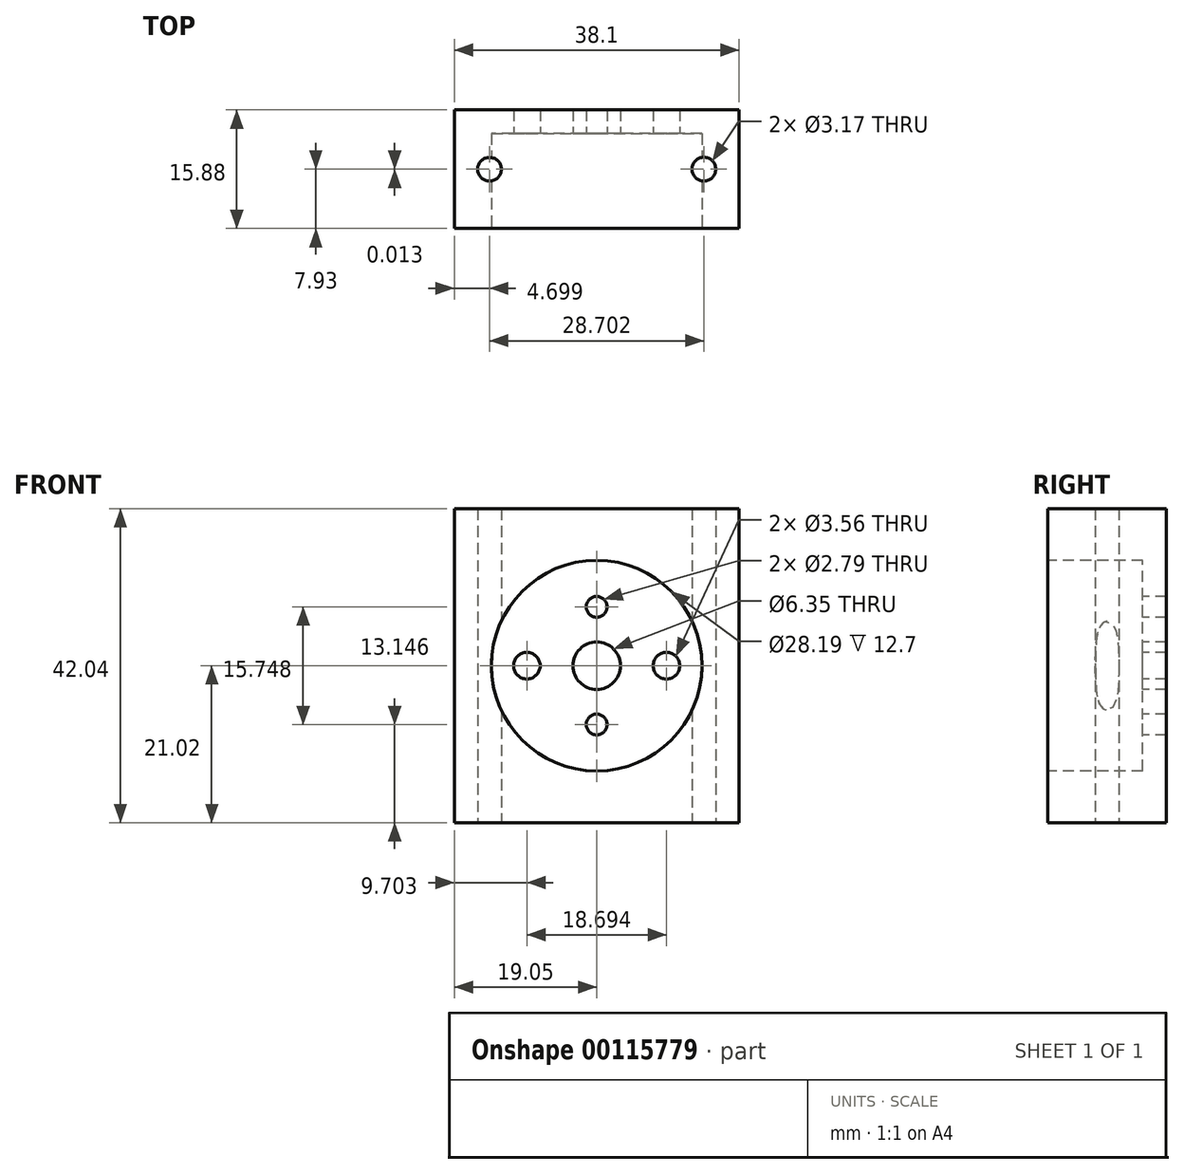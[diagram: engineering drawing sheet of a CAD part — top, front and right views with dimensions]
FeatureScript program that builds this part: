
annotation { "Feature Type Name" : "Feature", "Feature Type Description" : "" }
export const myFeature = defineFeature(function(context is Context, id is Id, definition is map)
    precondition{}
    {
        {
            var Q0;
            Q0=qCreatedBy(makeId("Front.planeOp"),FACE);
            var sketch = newSketch(context, id + "F0", { "sketchPlane" : qUnion([Q0])});
            skLineSegment(sketch, "E0.bottom", {"start": v(-19.05, 21.02) * mm, "end": v(19.05, 21.02) * mm});
            skLineSegment(sketch, "E0.top", {"start": v(-19.05, -21.02) * mm, "end": v(19.05, -21.02) * mm});
            skLineSegment(sketch, "E0.left", {"start": v(-19.05, 21.02) * mm, "end": v(-19.05, -21.02) * mm});
            skLineSegment(sketch, "E0.right", {"start": v(19.05, 21.02) * mm, "end": v(19.05, -21.02) * mm});
            skPoint(sketch, "E0.middle", {"position": v(0, 0) * mm});
            skSolve(sketch);
        }
        {
            var Q0;
            Q0=makeQuery(id+"F0.imprint","IMPRINT",FACE,{"disambiguationData":[TD([[makeQuery(id+"F0.imprint","IMPRINT",EDGE,{"derivedFrom":sQuery(id+"F0.wireOp",EDGE,"E0.bottom")}),-1.0]])]});
            extrude(context, id + "F1", {"entities" : qUnion([Q0]), "depth" : 15.88 * mm});
        }
        {
            var Q0;
            Q0=makeQuery(id+"F1.opExtrude","CAP_FACE",FACE,{"disambiguationData":[OSD([sQuery(id+"F0.wireOp",EDGE,"E0.bottom"),sQuery(id+"F0.wireOp",EDGE,"E0.top"),sQuery(id+"F0.wireOp",EDGE,"E0.left"),sQuery(id+"F0.wireOp",EDGE,"E0.right")])],"isStart":false});
            var sketch = newSketch(context, id + "F2", { "sketchPlane" : qUnion([Q0])});
            skCircle(sketch, "E1", {"center": v(0, 0) * mm, "radius": 3.18 * mm});
            skSolve(sketch);
        }
        {
            var Q0;
            Q0=makeQuery(id+"F2.imprint","IMPRINT",FACE,{"disambiguationData":[TD([[makeQuery(id+"F2.imprint","IMPRINT",EDGE,{"derivedFrom":sQuery(id+"F2.wireOp",EDGE,"E1")}),1.0]])]});
            extrude(context, id + "F3", {"entities" : qUnion([Q0]), "operationType" : NewBodyOperationType.REMOVE, "endBound" : BoundingType.THROUGH_ALL, "oppositeDirection" : true, "depth" : 25.4 * mm});
        }
        {
            var Q0;
            Q0=makeQuery(id+"F1.opExtrude","CAP_FACE",FACE,{"disambiguationData":[OSD([sQuery(id+"F0.wireOp",EDGE,"E0.bottom"),sQuery(id+"F0.wireOp",EDGE,"E0.top"),sQuery(id+"F0.wireOp",EDGE,"E0.left"),sQuery(id+"F0.wireOp",EDGE,"E0.right")])],"isStart":false});
            var sketch = newSketch(context, id + "F4", { "sketchPlane" : qUnion([Q0])});
            skCircle(sketch, "E2", {"center": v(0, 0) * mm, "radius": 14.1 * mm});
            skSolve(sketch);
        }
        {
            var Q0;
            Q0=makeQuery(id+"F4.imprint","IMPRINT",FACE,{"disambiguationData":[TD([[makeQuery(id+"F4.imprint","IMPRINT",EDGE,{"derivedFrom":sQuery(id+"F4.wireOp",EDGE,"E2")}),1.0]])]});
            extrude(context, id + "F5", {"entities" : qUnion([Q0]), "operationType" : NewBodyOperationType.REMOVE, "oppositeDirection" : true, "depth" : 12.7 * mm});
        }
        {
            var Q0;
            Q0=makeQuery(id+"F5.boolean.opBoolean","COPY",FACE,{"derivedFrom":makeQuery(id+"F5.opExtrude","CAP_FACE",FACE,{"disambiguationData":[OSD([sQuery(id+"F2.wireOp",EDGE,"E1"),sQuery(id+"F4.wireOp",EDGE,"E2")])],"isStart":false})});
            var sketch = newSketch(context, id + "F6", { "sketchPlane" : qUnion([Q0])});
            skCircle(sketch, "E3", {"center": v(9.35, 0) * mm, "radius": 1.78 * mm});
            skCircle(sketch, "E4", {"center": v(-9.35, 0) * mm, "radius": 1.78 * mm});
            skCircle(sketch, "E5", {"center": v(0, 7.87) * mm, "radius": 1.4 * mm});
            skCircle(sketch, "E6", {"center": v(0, -7.87) * mm, "radius": 1.4 * mm});
            skSolve(sketch);
        }
        {
            var Q0;
            Q0=makeQuery(id+"F6.imprint","IMPRINT",FACE,{"disambiguationData":[TD([[makeQuery(id+"F6.imprint","IMPRINT",EDGE,{"derivedFrom":sQuery(id+"F6.wireOp",EDGE,"E5")}),1.0]])]});
            var Q1;
            Q1=makeQuery(id+"F6.imprint","IMPRINT",FACE,{"disambiguationData":[TD([[makeQuery(id+"F6.imprint","IMPRINT",EDGE,{"derivedFrom":sQuery(id+"F6.wireOp",EDGE,"E4")}),1.0]])]});
            var Q2;
            Q2=makeQuery(id+"F6.imprint","IMPRINT",FACE,{"disambiguationData":[TD([[makeQuery(id+"F6.imprint","IMPRINT",EDGE,{"derivedFrom":sQuery(id+"F6.wireOp",EDGE,"E6")}),1.0]])]});
            var Q3;
            Q3=makeQuery(id+"F6.imprint","IMPRINT",FACE,{"disambiguationData":[TD([[makeQuery(id+"F6.imprint","IMPRINT",EDGE,{"derivedFrom":sQuery(id+"F6.wireOp",EDGE,"E3")}),1.0]])]});
            extrude(context, id + "F7", {"entities" : qUnion([Q0, Q1, Q2, Q3]), "operationType" : NewBodyOperationType.REMOVE, "endBound" : BoundingType.THROUGH_ALL, "oppositeDirection" : true, "depth" : 25.4 * mm});
        }
        {
            var Q0;
            Q0=makeQuery(id+"F1.opExtrude","SWEPT_FACE",FACE,{"disambiguationData":[OSD([sQuery(id+"F0.wireOp",EDGE,"E0.top")])]});
            var sketch = newSketch(context, id + "F8", { "sketchPlane" : qUnion([Q0])});
            skCircle(sketch, "E7", {"center": v(-14.35, 7.95) * mm, "radius": 1.59 * mm});
            skCircle(sketch, "E8", {"center": v(14.35, 7.94) * mm, "radius": 1.59 * mm});
            skPoint(sketch, "E8.centerSnap0", {"position": v(19.05, 7.94) * mm});
            skSolve(sketch);
        }
        {
            var Q0;
            Q0=qSketchRegion(id+"F8",true);
            extrude(context, id + "F9", {"entities" : qUnion([Q0]), "operationType" : NewBodyOperationType.REMOVE, "endBound" : BoundingType.THROUGH_ALL, "oppositeDirection" : true, "depth" : 25.4 * mm});
        }
    });
